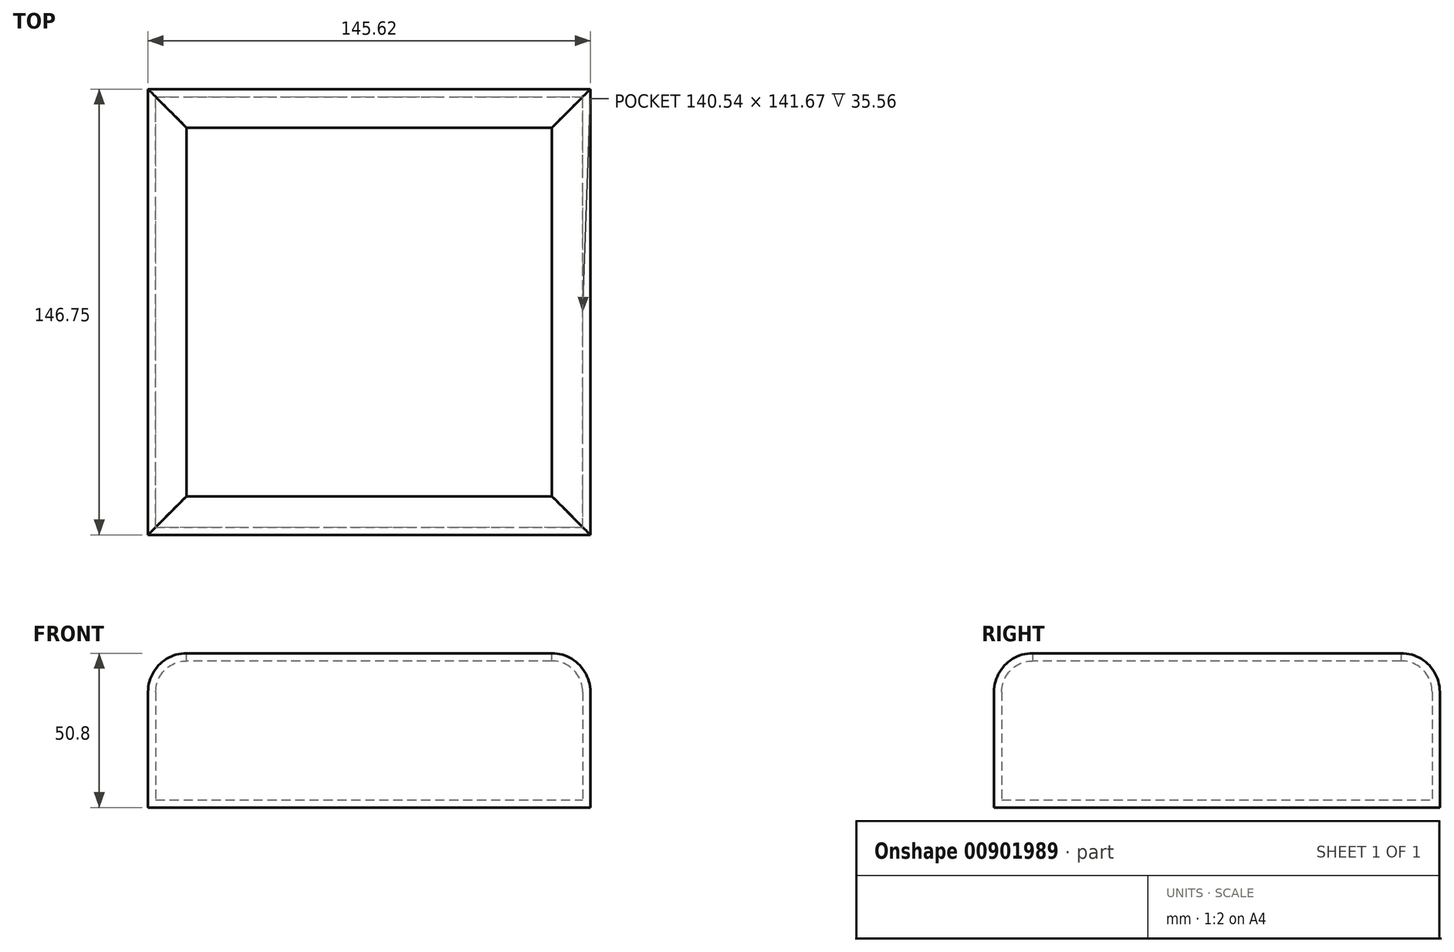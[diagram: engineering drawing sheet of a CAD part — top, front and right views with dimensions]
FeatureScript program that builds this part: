
annotation { "Feature Type Name" : "Feature", "Feature Type Description" : "" }
export const myFeature = defineFeature(function(context is Context, id is Id, definition is map)
    precondition{}
    {
        {
            var Q0;
            Q0=qCreatedBy(makeId("Top.planeOp"),FACE);
            var sketch = newSketch(context, id + "F0", { "sketchPlane" : qUnion([Q0])});
            skLineSegment(sketch, "E0.bottom", {"start": v(-72.78, -73.36) * mm, "end": v(72.84, -73.36) * mm});
            skLineSegment(sketch, "E0.top", {"start": v(-72.78, 73.39) * mm, "end": v(72.84, 73.39) * mm});
            skLineSegment(sketch, "E0.left", {"start": v(-72.78, -73.36) * mm, "end": v(-72.78, 73.39) * mm});
            skLineSegment(sketch, "E0.right", {"start": v(72.84, -73.36) * mm, "end": v(72.84, 73.39) * mm});
            skSolve(sketch);
        }
        {
            var Q0;
            Q0 = qSketchRegion(id + "F0", true);
            extrude(context, id + "F1", {"entities" : qUnion([Q0]), "depth" : 50.8 * mm, "offsetDistance" : 25.4 * mm});
        }
        {
            var Q0;
            Q0=makeQuery(id+"F1.opExtrude","CAP_EDGE",EDGE,{"disambiguationData":[OSD([sQuery(id+"F0.wireOp",EDGE,"E0.bottom")])],"isStart":false});
            var Q1;
            Q1=makeQuery(id+"F1.opExtrude","CAP_EDGE",EDGE,{"disambiguationData":[OSD([sQuery(id+"F0.wireOp",EDGE,"E0.right")])],"isStart":false});
            var Q2;
            Q2=makeQuery(id+"F1.opExtrude","CAP_EDGE",EDGE,{"disambiguationData":[OSD([sQuery(id+"F0.wireOp",EDGE,"E0.top")])],"isStart":false});
            var Q3;
            Q3=makeQuery(id+"F1.opExtrude","CAP_EDGE",EDGE,{"disambiguationData":[OSD([sQuery(id+"F0.wireOp",EDGE,"E0.left")])],"isStart":false});
            fillet(context, id + "F2", {"entities" : qUnion([Q0, Q1, Q2, Q3]), "radius" : 12.7 * mm, "tangentPropagation" : true, "allowEdgeOverflow" : false});
        }
        {
            var Q0;
            Q0=makeQuery(id+"F1.opExtrude","CAP_FACE",FACE,{"disambiguationData":[OSD([sQuery(id+"F0.wireOp",EDGE,"E0.bottom"),sQuery(id+"F0.wireOp",EDGE,"E0.top"),sQuery(id+"F0.wireOp",EDGE,"E0.left"),sQuery(id+"F0.wireOp",EDGE,"E0.right")])],"isStart":false});
            shell(context, id + "F3", {"entities" : qUnion([Q0]), "thickness" : 2.54 * mm});
        }
    });
